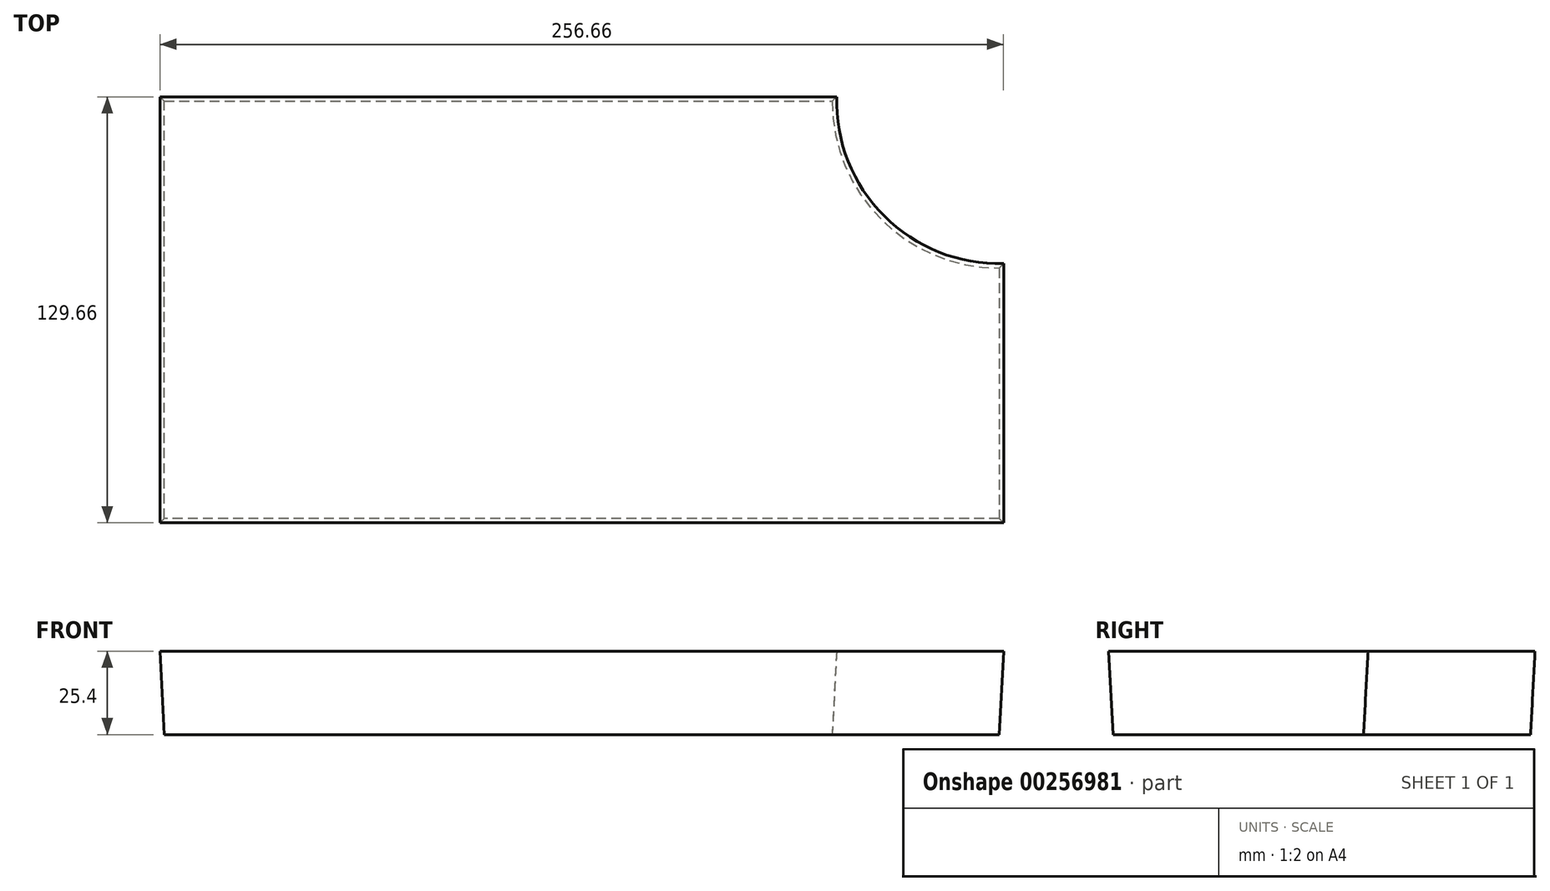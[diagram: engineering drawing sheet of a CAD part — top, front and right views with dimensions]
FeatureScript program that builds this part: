
annotation { "Feature Type Name" : "Feature", "Feature Type Description" : "" }
export const myFeature = defineFeature(function(context is Context, id is Id, definition is map)
    precondition{}
    {
        {
            var Q0;
            Q0=qCreatedBy(makeId("Top.planeOp"),FACE);
            var sketch = newSketch(context, id + "F0", { "sketchPlane" : qUnion([Q0])});
            skLineSegment(sketch, "E0.bottom", {"start": v(76.2, 63.5) * mm, "end": v(-127, 63.5) * mm});
            skLineSegment(sketch, "E0.top", {"start": v(127, -63.5) * mm, "end": v(-127, -63.5) * mm});
            skLineSegment(sketch, "E0.left", {"start": v(127, 12.7) * mm, "end": v(127, -63.5) * mm});
            skLineSegment(sketch, "E0.right", {"start": v(-127, 63.5) * mm, "end": v(-127, -63.5) * mm});
            skPoint(sketch, "E0.middle", {"position": v(0, 0) * mm});
            skArc(sketch, "E1", {"start": v(76.2, 63.5) * mm, "mid": v(91.08, 27.58) * mm, "end": v(127, 12.7) * mm});
            skSolve(sketch);
        }
        {
            var Q0;
            Q0=makeQuery(id+"F0.imprint","IMPRINT",FACE,{"disambiguationData":[TD([[makeQuery(id+"F0.imprint","IMPRINT",EDGE,{"derivedFrom":sQuery(id+"F0.wireOp",EDGE,"E0.bottom")}),1.0]])]});
            extrude(context, id + "F1", {"entities" : qUnion([Q0]), "depth" : 25.4 * mm, "hasDraft" : true, "draftAngle" : 3 * degree});
        }
    });
